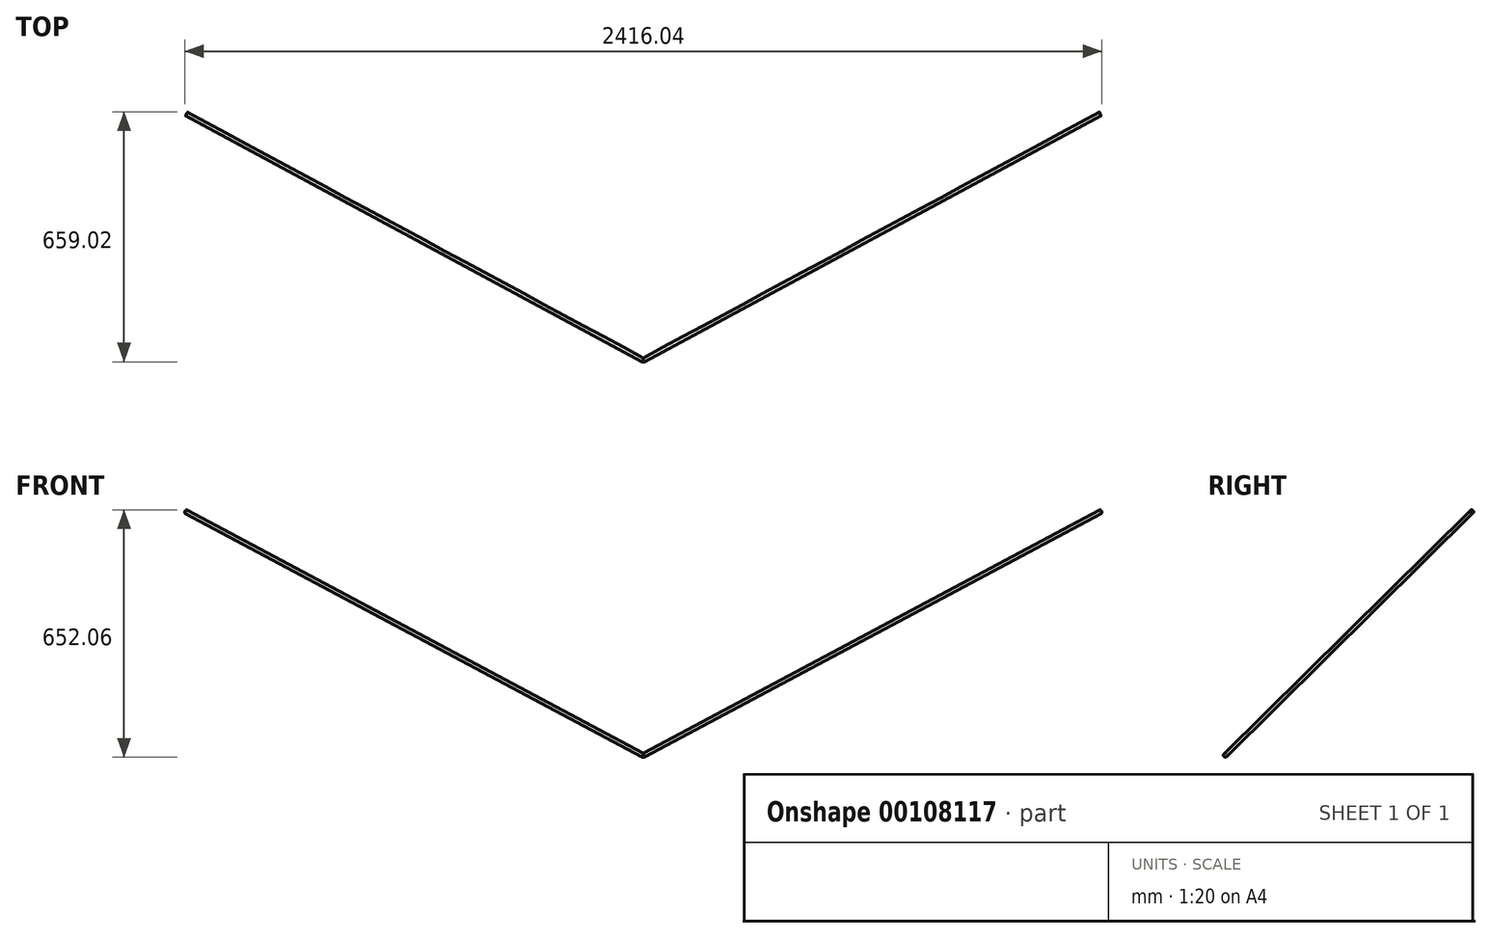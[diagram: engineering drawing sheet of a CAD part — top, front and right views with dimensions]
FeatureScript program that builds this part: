
annotation { "Feature Type Name" : "Feature", "Feature Type Description" : "" }
export const myFeature = defineFeature(function(context is Context, id is Id, definition is map)
    precondition{}
    {
        {
            assignVariable(context, id + "F0", {"name" : "Y1", "anyValue" : 0});
        }
        {
            var Q0;
            Q0=qCreatedBy(makeId("Front.planeOp"),FACE);
            cPlane(context, id + "F1", {"entities" : qUnion([Q0]), "cplaneType" : CPlaneType.OFFSET, "offset" : (getVariable(context, 'Y1')) * mm, "width" : 150 * mm, "height" : 150 * mm});
        }
        {
            var Q0;
            Q0=qCreatedBy(id+"F1.planeOp",FACE);
            var sketch = newSketch(context, id + "F2", { "sketchPlane" : qUnion([Q0])});
            skPoint(sketch, "E0", {"position": v(-1205, 5300) * mm});
            skPoint(sketch, "E1", {"position": v(-1205, 0) * mm});
            skSolve(sketch);
        }
        {
            assignVariable(context, id + "F3", {"name" : "Y2", "anyValue" : 3900 / 2 - 2 * 650});
        }
        {
            var Q0;
            Q0=qCreatedBy(makeId("Front.planeOp"),FACE);
            cPlane(context, id + "F4", {"entities" : qUnion([Q0]), "cplaneType" : CPlaneType.OFFSET, "offset" : (getVariable(context, 'Y2')) * mm, "width" : 150 * mm, "height" : 150 * mm});
        }
        {
            var Q0;
            Q0=qCreatedBy(id+"F4.planeOp",FACE);
            var sketch = newSketch(context, id + "F5", { "sketchPlane" : qUnion([Q0])});
            skPoint(sketch, "E2", {"position": v(0, 4657) * mm});
            skSolve(sketch);
        }
        {
            var Q0;
            Q0=sQuery(id+"F2.wireOp",VERTEX,"E0");
            var Q1;
            Q1=sQuery(id+"F2.wireOp",VERTEX,"E1");
            var Q2;
            Q2=sQuery(id+"F5.wireOp",VERTEX,"E2");
            cPlane(context, id + "F6", {"entities" : qUnion([Q0, Q1, Q2]), "cplaneType" : CPlaneType.THREE_POINT, "offset" : 25 * mm, "width" : 150 * mm, "height" : 150 * mm});
        }
        {
            var Q0;
            Q0=qCreatedBy(id+"F6.planeOp",FACE);
            var sketch = newSketch(context, id + "F7", { "sketchPlane" : qUnion([Q0])});
            skPoint(sketch, "E3.0", {"position": v(1060.54, 5300) * mm});
            skPoint(sketch, "E4.0", {"position": v(-308.59, 4657) * mm});
            skLineSegment(sketch, "E5", {"start": v(1060.54, 5300) * mm, "end": v(-308.59, 4657) * mm});
            skSolve(sketch);
        }
        {
            var Q0;
            Q0=sQuery(id+"F7.wireOp",VERTEX,"E3.0");
            var Q1;
            Q1=sQuery(id+"F7.wireOp",EDGE,"E5");
            cPlane(context, id + "F8", {"entities" : qUnion([Q0, Q1]), "cplaneType" : CPlaneType.LINE_POINT, "offset" : 25 * mm, "width" : 150 * mm, "height" : 150 * mm});
        }
        {
            var Q0;
            Q0=qCreatedBy(id+"F8.planeOp",FACE);
            var sketch = newSketch(context, id + "F9", { "sketchPlane" : qUnion([Q0])});
            skPoint(sketch, "E6.0", {"position": v(-1529.05, 4108.65) * mm});
            skCircle(sketch, "E7", {"center": v(-1529.05, 4108.65) * mm, "radius": 5 * mm});
            skSolve(sketch);
        }
        {
            var Q0;
            Q0=makeQuery(id+"F9.imprint","IMPRINT",FACE,{"disambiguationData":[TD([[makeQuery(id+"F9.imprint","IMPRINT",EDGE,{"derivedFrom":sQuery(id+"F9.wireOp",EDGE,"E7")}),1.0]])]});
            var Q1;
            Q1=sQuery(id+"F7.wireOp",EDGE,"E5");
            sweep(context, id + "F10", {"profiles" : qUnion([Q0]), "path" : qUnion([Q1])});
        }
        {
            var Q0;
            Q0=makeQuery(id+"F10.opSweep","SWEPT_BODY",BODY,{"disambiguationData":[OSD([sQuery(id+"F7.wireOp",EDGE,"E5"),sQuery(id+"F9.wireOp",EDGE,"E7")])]});
            var Q1;
            Q1=qCreatedBy(makeId("Right.planeOp"),FACE);
            mirror(context, id + "F11", {"operationType" : NewBodyOperationType.ADD, "entities" : qUnion([Q0]), "mirrorPlane" : qUnion([Q1])});
        }
    });
